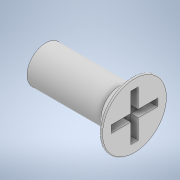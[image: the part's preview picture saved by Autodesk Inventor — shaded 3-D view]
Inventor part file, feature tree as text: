
AUTODESK INVENTOR PART (.ipt)
format: ipt  version: 2023 (Build 270158000, 158)  size: 136,192 bytes
history: native  units: mm
features: sketch x2, revolve x1, fillet x1, extrude x1, projected_geometry x1
ambient origin geometry x8: Origin, YZ Plane, XZ Plane, XY Plane, X Axis, Y Axis, Z Axis, Center Point
bodies: Solid1 (feature_tree)
feature tree (6):
  revolve  "Revolution1"  [1 undecoded]
  fillet  "Fillet1"  Radius=4.0mm
  extrude  "Extrusion1"  TaperAngle=90.0deg  [1 undecoded]
  sketch  "Sketch1"  dims[d0=1.85mm d1=0.8mm d2=4.0mm]
  sketch  "Sketch2"  dims[d3=1.0mm d4=90.0deg d5=0.05mm d6=0.4mm d7=2.5mm d8=0.4mm d9=2.5mm d10=0.4mm d11=0.0mm]
  projected_geometry  "Projected Loop1"
note: 2 required parameter values undecoded (feature->parameter linkage not recoverable at this tier; creation-order binding heuristic only, values carry confidence <= 0.55)